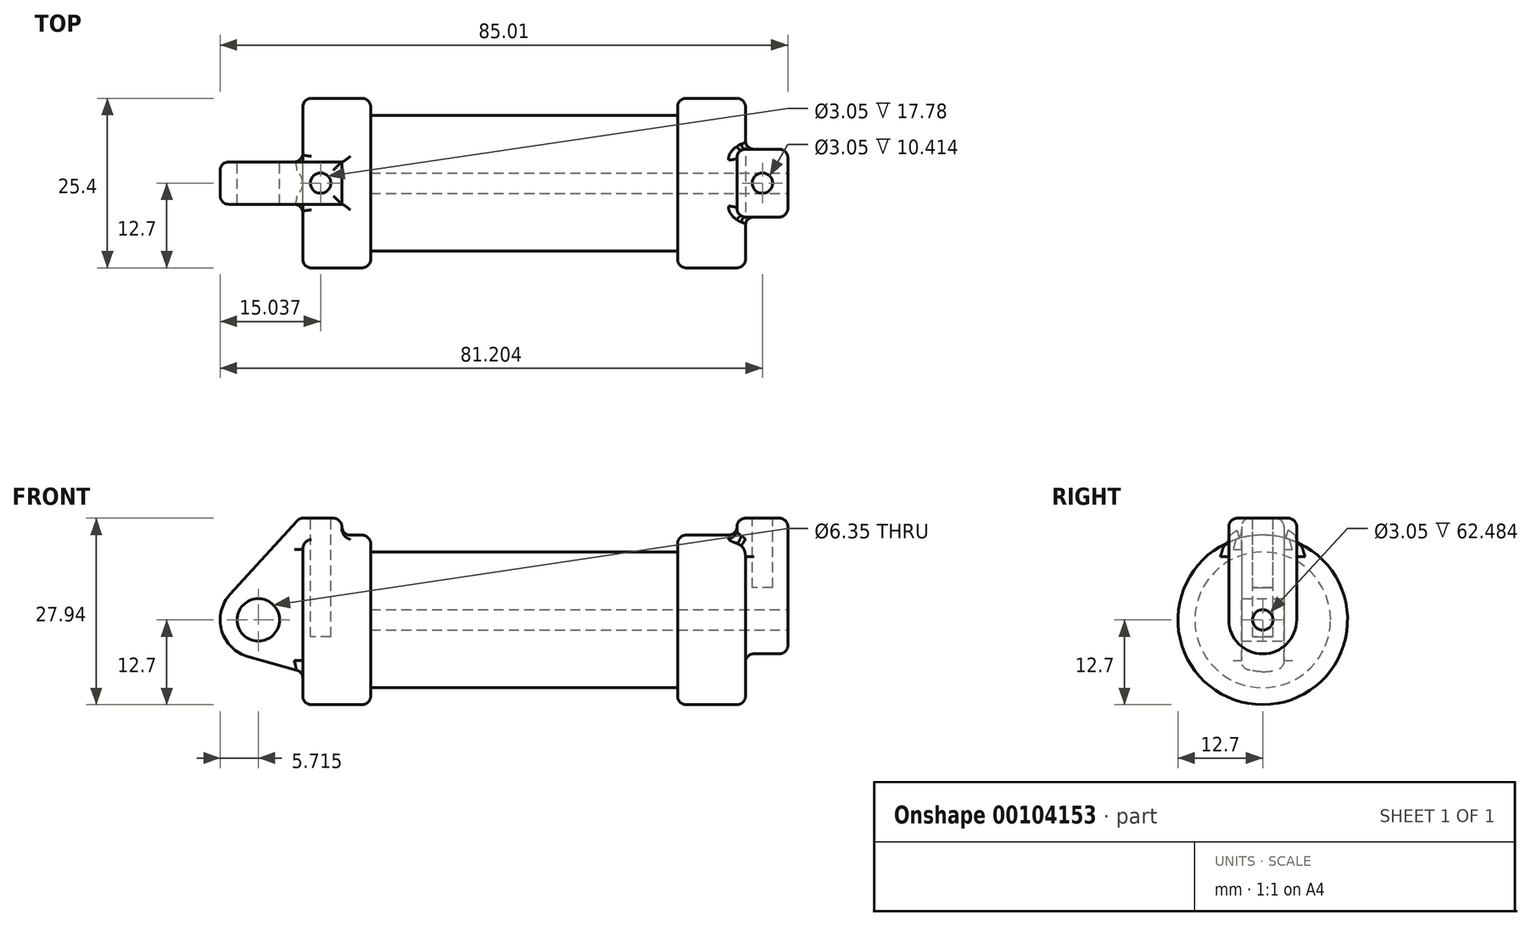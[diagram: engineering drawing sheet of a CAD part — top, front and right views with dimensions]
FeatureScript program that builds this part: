
annotation { "Feature Type Name" : "Feature", "Feature Type Description" : "" }
export const myFeature = defineFeature(function(context is Context, id is Id, definition is map)
    precondition{}
    {
        {
            var Q0;
            Q0=qCreatedBy(makeId("Front.planeOp"),FACE);
            var sketch = newSketch(context, id + "F0", { "sketchPlane" : qUnion([Q0])});
            skLineSegment(sketch, "E0", {"start": v(0, 0) * mm, "end": v(0, 12.7) * mm});
            skLineSegment(sketch, "E1", {"start": v(0, 12.7) * mm, "end": v(10.16, 12.7) * mm});
            skLineSegment(sketch, "E2", {"start": v(10.16, 12.7) * mm, "end": v(10.16, 10.16) * mm});
            skLineSegment(sketch, "E3", {"start": v(10.16, 10.16) * mm, "end": v(56.13, 10.16) * mm});
            skLineSegment(sketch, "E4", {"start": v(56.13, 10.16) * mm, "end": v(56.13, 12.7) * mm});
            skLineSegment(sketch, "E5", {"start": v(56.13, 12.7) * mm, "end": v(66.3, 12.7) * mm});
            skLineSegment(sketch, "E6", {"start": v(66.3, 12.7) * mm, "end": v(66.3, 0) * mm});
            skLineSegment(sketch, "E7", {"start": v(66.3, 0) * mm, "end": v(0, 0) * mm});
            skLineSegment(sketch, "E8", {"start": v(5.84, 15.24) * mm, "end": v(-0.5, 15.24) * mm});
            skLineSegment(sketch, "E9", {"start": v(-0.5, 15.24) * mm, "end": v(-10.88, 3.85) * mm});
            skLineSegment(sketch, "E10", {"start": v(0, 0) * mm, "end": v(-6.65, 0) * mm});
            skCircle(sketch, "E11", {"center": v(-6.65, 0) * mm, "radius": 5.72 * mm});
            skCircle(sketch, "E12", {"center": v(-6.65, 0) * mm, "radius": 3.18 * mm});
            skLineSegment(sketch, "E13", {"start": v(5.84, 15.24) * mm, "end": v(5.84, -9.4) * mm});
            skLineSegment(sketch, "E14", {"start": v(5.84, -9.4) * mm, "end": v(-8.18, -5.5) * mm});
            skSolve(sketch);
        }
        {
            var Q0;
            {var subQ0=sQuery(id+"F0.wireOp",EDGE,"E2");Q0=makeQuery(id+"F0.imprint","IMPRINT",FACE,{"disambiguationData":[TD([[makeQuery(id+"F0.imprint","IMPRINT",EDGE,{"derivedFrom":subQ0}),-1.0]])]});}
            var Q1;
            {var subQ0=sQuery(id+"F0.wireOp",EDGE,"E0");Q1=makeQuery(id+"F0.imprint","IMPRINT",FACE,{"disambiguationData":[TD([[makeQuery(id+"F0.imprint","IMPRINT",EDGE,{"derivedFrom":subQ0}),-1.0]])]});}
            var Q2;
            Q2=sQuery(id+"F0.wireOp",EDGE,"E7");
            revolve(context, id + "F1", {"entities" : qUnion([Q0, Q1]), "axis" : qUnion([Q2]), "revolveType" : RevolveType.FULL});
        }
        {
            var Q0;
            {var subQ0=sQuery(id+"F0.wireOp",EDGE,"E0");Q0=makeQuery(id+"F0.imprint","IMPRINT",FACE,{"disambiguationData":[TD([[makeQuery(id+"F0.imprint","IMPRINT",EDGE,{"derivedFrom":subQ0}),-1.0]])]});}
            var Q1;
            {var subQ3=sQuery(id+"F0.wireOp",EDGE,"E0");Q1=makeQuery(id+"F0.imprint","IMPRINT",FACE,{"disambiguationData":[TD([[makeQuery(id+"F0.imprint","IMPRINT",EDGE,{"derivedFrom":subQ3}),1.0]])]});}
            var Q2;
            {var subQ0=sQuery(id+"F0.wireOp",EDGE,"E14");Q2=makeQuery(id+"F0.imprint","IMPRINT",FACE,{"disambiguationData":[TD([[makeQuery(id+"F0.imprint","IMPRINT",EDGE,{"derivedFrom":subQ0}),-1.0]])]});}
            var Q3;
            {var subQ4=sQuery(id+"F0.wireOp",EDGE,"E12");Q3=makeQuery(id+"F0.imprint","IMPRINT",FACE,{"disambiguationData":[TD([[makeQuery(id+"F0.imprint","IMPRINT",EDGE,{"derivedFrom":subQ4}),-1.0]])]});}
            extrude(context, id + "F2", {"entities" : qUnion([Q0, Q1, Q2, Q3]), "operationType" : NewBodyOperationType.ADD, "endBound" : BoundingType.SYMMETRIC, "depth" : 6.35 * mm});
        }
        {
            var Q0;
            Q0=makeQuery(id+"F1.opRevolve","SWEPT_FACE",FACE,{"disambiguationData":[OSD([sQuery(id+"F0.wireOp",EDGE,"E6")])]});
            var sketch = newSketch(context, id + "F3", { "sketchPlane" : qUnion([Q0])});
            skCircle(sketch, "E15", {"center": v(0, 0) * mm, "radius": 1.52 * mm});
            skCircle(sketch, "E16", {"center": v(0, 0) * mm, "radius": 5.08 * mm});
            skLineSegment(sketch, "E17", {"start": v(-5.08, 0) * mm, "end": v(-5.08, 15.24) * mm});
            skLineSegment(sketch, "E18", {"start": v(5.08, 0) * mm, "end": v(5.08, 15.24) * mm});
            skLineSegment(sketch, "E19", {"start": v(-5.08, 15.24) * mm, "end": v(5.08, 15.24) * mm});
            skSolve(sketch);
        }
        {
            var Q0;
            Q0 = qSketchRegion(id + "F3", true);
            extrude(context, id + "F4", {"entities" : qUnion([Q0]), "operationType" : NewBodyOperationType.ADD, "oppositeDirection" : true, "depth" : 1.27 * mm, "hasSecondDirection" : true, "secondDirectionOppositeDirection" : false, "secondDirectionDepth" : 6.35 * mm});
        }
        {
            var Q0;
            Q0=makeQuery(id+"F4.boolean.opBoolean","SPLIT",FACE,{"disambiguationData":[TD([makeQuery(id+"F4.opExtrude","SWEPT_FACE",FACE,{"disambiguationData":[OSD([sQuery(id+"F3.wireOp",EDGE,"E15")])]})])],"derivedFrom":makeQuery(id+"F1.opRevolve","SWEPT_FACE",FACE,{"disambiguationData":[OSD([sQuery(id+"F0.wireOp",EDGE,"E6")])]})});
            var Q1;
            Q1=makeQuery(id+"F1.opRevolve","SWEPT_FACE",FACE,{"disambiguationData":[OSD([sQuery(id+"F0.wireOp",EDGE,"E2")])]});
            extrude(context, id + "F5", {"entities" : qUnion([Q0]), "operationType" : NewBodyOperationType.REMOVE, "endBound" : BoundingType.UP_TO_SURFACE, "oppositeDirection" : true, "endBoundEntityFace" : qUnion([Q1]), "depth" : 25.4 * mm});
        }
        {
            var Q0;
            Q0=makeQuery(id+"F2.opExtrude","SWEPT_FACE",FACE,{"disambiguationData":[OSD([sQuery(id+"F0.wireOp",EDGE,"E8")])]});
            var sketch = newSketch(context, id + "F6", { "sketchPlane" : qUnion([Q0])});
            skCircle(sketch, "E20", {"center": v(2.67, 0) * mm, "radius": 1.52 * mm});
            skLineSegment(sketch, "E21", {"start": v(2.67, 3.18) * mm, "end": v(2.67, 1.52) * mm});
            skLineSegment(sketch, "E22.trimOffspring", {"start": v(2.67, -1.52) * mm, "end": v(2.67, -3.18) * mm});
            skSolve(sketch);
        }
        {
            var Q0;
            Q0=makeQuery(id+"F4.opExtrude","SWEPT_FACE",FACE,{"disambiguationData":[OSD([sQuery(id+"F3.wireOp",EDGE,"E19")])]});
            var sketch = newSketch(context, id + "F7", { "sketchPlane" : qUnion([Q0])});
            skLineSegment(sketch, "E23", {"start": v(68.83, 5.08) * mm, "end": v(68.83, 1.52) * mm});
            skCircle(sketch, "E24", {"center": v(68.83, 0) * mm, "radius": 1.52 * mm});
            skLineSegment(sketch, "E25.trimOffspring", {"start": v(68.83, -1.52) * mm, "end": v(68.83, -5.08) * mm});
            skPoint(sketch, "E26.start.orphan", {"position": v(65.02, 0) * mm});
            skPoint(sketch, "E27.trimOffspring.end.orphan", {"position": v(72.64, 0) * mm});
            skSolve(sketch);
        }
        {
            var Q0;
            Q0 = qSketchRegion(id + "F6", true);
            extrude(context, id + "F8", {"entities" : qUnion([Q0]), "operationType" : NewBodyOperationType.REMOVE, "oppositeDirection" : true, "depth" : 17.78 * mm});
        }
        {
            var Q0;
            Q0 = qSketchRegion(id + "F7", true);
            extrude(context, id + "F9", {"entities" : qUnion([Q0]), "operationType" : NewBodyOperationType.REMOVE, "oppositeDirection" : true, "depth" : 10.4 * mm});
        }
        {
            var Q0;
            Q0=makeQuery(id+"F1.opRevolve","SWEPT_EDGE",EDGE,{"disambiguationData":[OSD([sQuery(id+"F0.wireOp",EDGE,"E0"),sQuery(id+"F0.wireOp",EDGE,"E1")])]});
            var Q1;
            Q1=makeQuery(id+"F1.opRevolve","SWEPT_EDGE",EDGE,{"disambiguationData":[OSD([sQuery(id+"F0.wireOp",EDGE,"E1"),sQuery(id+"F0.wireOp",EDGE,"E2")])]});
            var Q2;
            Q2=makeQuery(id+"F1.opRevolve","SWEPT_EDGE",EDGE,{"disambiguationData":[OSD([sQuery(id+"F0.wireOp",EDGE,"E4"),sQuery(id+"F0.wireOp",EDGE,"E5")])]});
            var Q3;
            Q3=makeQuery(id+"F1.opRevolve","SWEPT_EDGE",EDGE,{"disambiguationData":[OSD([sQuery(id+"F0.wireOp",EDGE,"E5"),sQuery(id+"F0.wireOp",EDGE,"E6")])]});
            fillet(context, id + "F10", {"entities" : qUnion([Q0, Q1, Q2, Q3]), "radius" : 1.27 * mm, "tangentPropagation" : true, "allowEdgeOverflow" : false});
        }
        {
            var Q0;
            Q0=makeQuery(id+"F2.boolean.opBoolean","INTERSECT",EDGE,{"derivedFrom":[makeQuery(id+"F1.opRevolve","SWEPT_FACE",FACE,{"disambiguationData":[OSD([sQuery(id+"F0.wireOp",EDGE,"E1")])]}),makeQuery(id+"F2.opExtrude","CAP_FACE",FACE,{"disambiguationData":[OSD([sQuery(id+"F0.wireOp",EDGE,"E8"),sQuery(id+"F0.wireOp",EDGE,"E9"),sQuery(id+"F0.wireOp",EDGE,"E11"),sQuery(id+"F0.wireOp",EDGE,"E12"),sQuery(id+"F0.wireOp",EDGE,"E13"),sQuery(id+"F0.wireOp",EDGE,"E14")])],"isStart":false})]});
            var Q1;
            Q1=makeQuery(id+"F2.opExtrude","CAP_EDGE",EDGE,{"disambiguationData":[OSD([sQuery(id+"F0.wireOp",EDGE,"E8")])],"isStart":false});
            var Q2;
            Q2=makeQuery(id+"F2.opExtrude","CAP_EDGE",EDGE,{"disambiguationData":[OSD([sQuery(id+"F0.wireOp",EDGE,"E9")])],"isStart":false});
            var Q3;
            Q3=makeQuery(id+"F2.opExtrude","CAP_EDGE",EDGE,{"disambiguationData":[OSD([sQuery(id+"F0.wireOp",EDGE,"E11")])],"isStart":false});
            var Q4;
            Q4=makeQuery(id+"F2.opExtrude","CAP_EDGE",EDGE,{"disambiguationData":[OSD([sQuery(id+"F0.wireOp",EDGE,"E14")])],"isStart":false});
            var Q5;
            Q5=makeQuery(id+"F2.opExtrude","SWEPT_EDGE",EDGE,{"disambiguationData":[OSD([sQuery(id+"F0.wireOp",EDGE,"E8"),sQuery(id+"F0.wireOp",EDGE,"E13")])]});
            var Q6;
            Q6=makeQuery(id+"F2.boolean.opBoolean","INTERSECT",EDGE,{"derivedFrom":[makeQuery(id+"F1.opRevolve","SWEPT_FACE",FACE,{"disambiguationData":[OSD([sQuery(id+"F0.wireOp",EDGE,"E1")])]}),makeQuery(id+"F2.opExtrude","SWEPT_FACE",FACE,{"disambiguationData":[OSD([sQuery(id+"F0.wireOp",EDGE,"E13")])]})]});
            var Q7;
            Q7=makeQuery(id+"F2.opExtrude","CAP_EDGE",EDGE,{"disambiguationData":[OSD([sQuery(id+"F0.wireOp",EDGE,"E8")])],"isStart":true});
            var Q8;
            Q8=makeQuery(id+"F2.boolean.opBoolean","INTERSECT",EDGE,{"derivedFrom":[makeQuery(id+"F1.opRevolve","SWEPT_FACE",FACE,{"disambiguationData":[OSD([sQuery(id+"F0.wireOp",EDGE,"E1")])]}),makeQuery(id+"F2.opExtrude","CAP_FACE",FACE,{"disambiguationData":[OSD([sQuery(id+"F0.wireOp",EDGE,"E8"),sQuery(id+"F0.wireOp",EDGE,"E9"),sQuery(id+"F0.wireOp",EDGE,"E11"),sQuery(id+"F0.wireOp",EDGE,"E12"),sQuery(id+"F0.wireOp",EDGE,"E13"),sQuery(id+"F0.wireOp",EDGE,"E14")])],"isStart":true})]});
            var Q9;
            Q9=makeQuery(id+"F2.opExtrude","CAP_EDGE",EDGE,{"disambiguationData":[OSD([sQuery(id+"F0.wireOp",EDGE,"E9")])],"isStart":true});
            var Q10;
            Q10=makeQuery(id+"F2.opExtrude","CAP_EDGE",EDGE,{"disambiguationData":[OSD([sQuery(id+"F0.wireOp",EDGE,"E11")])],"isStart":true});
            var Q11;
            Q11=makeQuery(id+"F2.opExtrude","CAP_EDGE",EDGE,{"disambiguationData":[OSD([sQuery(id+"F0.wireOp",EDGE,"E14")])],"isStart":true});
            var Q12;
            Q12=makeQuery(id+"F10.opFillet","BLEND_EDGE",EDGE,{"blendedFrom":[makeQuery(id+"F1.opRevolve","SWEPT_EDGE",EDGE,{"disambiguationData":[OSD([sQuery(id+"F0.wireOp",EDGE,"E0"),sQuery(id+"F0.wireOp",EDGE,"E1")])]}),makeQuery(id+"F2.opExtrude","CAP_FACE",FACE,{"disambiguationData":[OSD([sQuery(id+"F0.wireOp",EDGE,"E8"),sQuery(id+"F0.wireOp",EDGE,"E9"),sQuery(id+"F0.wireOp",EDGE,"E11"),sQuery(id+"F0.wireOp",EDGE,"E12"),sQuery(id+"F0.wireOp",EDGE,"E13"),sQuery(id+"F0.wireOp",EDGE,"E14")])],"isStart":true})],"blendedInto":[makeQuery(id+"F2.opExtrude","CAP_FACE",FACE,{"disambiguationData":[OSD([sQuery(id+"F0.wireOp",EDGE,"E8"),sQuery(id+"F0.wireOp",EDGE,"E9"),sQuery(id+"F0.wireOp",EDGE,"E11"),sQuery(id+"F0.wireOp",EDGE,"E12"),sQuery(id+"F0.wireOp",EDGE,"E13"),sQuery(id+"F0.wireOp",EDGE,"E14")])],"isStart":true})]});
            var Q13;
            Q13=makeQuery(id+"F2.boolean.opBoolean","INTERSECT",EDGE,{"derivedFrom":[makeQuery(id+"F1.opRevolve","SWEPT_FACE",FACE,{"disambiguationData":[OSD([sQuery(id+"F0.wireOp",EDGE,"E0")])]}),makeQuery(id+"F2.opExtrude","CAP_FACE",FACE,{"disambiguationData":[OSD([sQuery(id+"F0.wireOp",EDGE,"E8"),sQuery(id+"F0.wireOp",EDGE,"E9"),sQuery(id+"F0.wireOp",EDGE,"E11"),sQuery(id+"F0.wireOp",EDGE,"E12"),sQuery(id+"F0.wireOp",EDGE,"E13"),sQuery(id+"F0.wireOp",EDGE,"E14")])],"isStart":true})]});
            var Q14;
            Q14=makeQuery(id+"F2.opExtrude","SWEPT_EDGE",EDGE,{"disambiguationData":[OSD([sQuery(id+"F0.wireOp",EDGE,"E8"),sQuery(id+"F0.wireOp",EDGE,"E9")])]});
            fillet(context, id + "F11", {"entities" : qUnion([Q0, Q1, Q2, Q3, Q4, Q5, Q6, Q7, Q8, Q9, Q10, Q11, Q12, Q13, Q14]), "radius" : 1.27 * mm, "tangentPropagation" : true, "allowEdgeOverflow" : false});
        }
        {
            var Q0;
            Q0=makeQuery(id+"F4.opExtrude","CAP_EDGE",EDGE,{"disambiguationData":[OSD([sQuery(id+"F3.wireOp",EDGE,"E18")])],"isStart":true});
            var Q1;
            Q1=makeQuery(id+"F4.opExtrude","CAP_EDGE",EDGE,{"disambiguationData":[OSD([sQuery(id+"F3.wireOp",EDGE,"E19")])],"isStart":true});
            var Q2;
            Q2=makeQuery(id+"F4.opExtrude","SWEPT_EDGE",EDGE,{"disambiguationData":[OSD([sQuery(id+"F3.wireOp",EDGE,"E17"),sQuery(id+"F3.wireOp",EDGE,"E19")])]});
            var Q3;
            Q3=makeQuery(id+"F4.opExtrude","SWEPT_EDGE",EDGE,{"disambiguationData":[OSD([sQuery(id+"F3.wireOp",EDGE,"E18"),sQuery(id+"F3.wireOp",EDGE,"E19")])]});
            var Q4;
            Q4=makeQuery(id+"F4.opExtrude","CAP_EDGE",EDGE,{"disambiguationData":[OSD([sQuery(id+"F3.wireOp",EDGE,"E19")])],"isStart":false});
            var Q5;
            Q5=makeQuery(id+"F4.boolean.opBoolean","INTERSECT",EDGE,{"derivedFrom":[makeQuery(id+"F1.opRevolve","SWEPT_FACE",FACE,{"disambiguationData":[OSD([sQuery(id+"F0.wireOp",EDGE,"E5")])]}),makeQuery(id+"F4.opExtrude","CAP_FACE",FACE,{"disambiguationData":[OSD([sQuery(id+"F3.wireOp",EDGE,"E15"),sQuery(id+"F3.wireOp",EDGE,"E16"),sQuery(id+"F3.wireOp",EDGE,"E17"),sQuery(id+"F3.wireOp",EDGE,"E18"),sQuery(id+"F3.wireOp",EDGE,"E19")])],"isStart":false})]});
            var Q6;
            Q6=makeQuery(id+"F4.opExtrude","CAP_EDGE",EDGE,{"disambiguationData":[OSD([sQuery(id+"F3.wireOp",EDGE,"E18")])],"isStart":false});
            var Q7;
            Q7=makeQuery(id+"F4.opExtrude","CAP_EDGE",EDGE,{"disambiguationData":[OSD([sQuery(id+"F3.wireOp",EDGE,"E17")])],"isStart":false});
            var Q8;
            Q8=makeQuery(id+"F4.opExtrude","CAP_EDGE",EDGE,{"disambiguationData":[OSD([sQuery(id+"F3.wireOp",EDGE,"E17")])],"isStart":true});
            var Q9;
            Q9=makeQuery(id+"F4.opExtrude","CAP_EDGE",EDGE,{"disambiguationData":[OSD([sQuery(id+"F3.wireOp",EDGE,"E16")])],"isStart":true});
            var Q10;
            Q10=makeQuery(id+"F10.opFillet","BLEND_EDGE",EDGE,{"blendedFrom":[makeQuery(id+"F1.opRevolve","SWEPT_EDGE",EDGE,{"disambiguationData":[OSD([sQuery(id+"F0.wireOp",EDGE,"E5"),sQuery(id+"F0.wireOp",EDGE,"E6")])]}),makeQuery(id+"F4.opExtrude","SWEPT_FACE",FACE,{"disambiguationData":[OSD([sQuery(id+"F3.wireOp",EDGE,"E17")])]})],"blendedInto":[makeQuery(id+"F4.opExtrude","SWEPT_FACE",FACE,{"disambiguationData":[OSD([sQuery(id+"F3.wireOp",EDGE,"E17")])]})]});
            var Q11;
            Q11=makeQuery(id+"F4.boolean.opBoolean","INTERSECT",EDGE,{"derivedFrom":[makeQuery(id+"F1.opRevolve","SWEPT_FACE",FACE,{"disambiguationData":[OSD([sQuery(id+"F0.wireOp",EDGE,"E6")])]}),makeQuery(id+"F4.opExtrude","SWEPT_FACE",FACE,{"disambiguationData":[OSD([sQuery(id+"F3.wireOp",EDGE,"E17")])]})]});
            fillet(context, id + "F12", {"entities" : qUnion([Q0, Q1, Q2, Q3, Q4, Q5, Q6, Q7, Q8, Q9, Q10, Q11]), "radius" : 1.27 * mm, "tangentPropagation" : true, "allowEdgeOverflow" : false});
        }
    });
